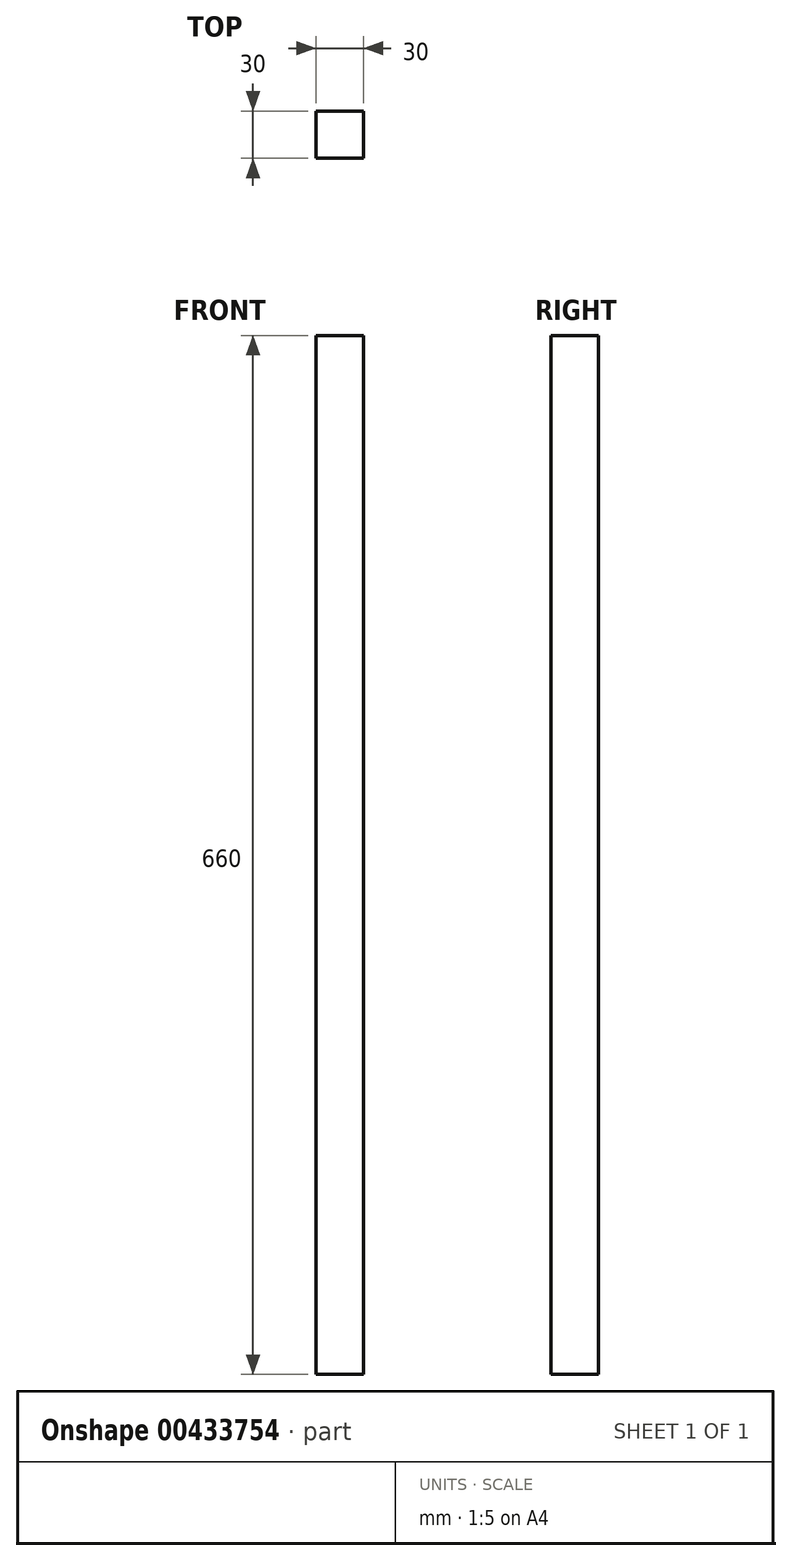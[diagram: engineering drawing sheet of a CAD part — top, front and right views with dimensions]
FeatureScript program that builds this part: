
annotation { "Feature Type Name" : "Feature", "Feature Type Description" : "" }
export const myFeature = defineFeature(function(context is Context, id is Id, definition is map)
    precondition{}
    {
        {
            var Q0;
            Q0=qCreatedBy(makeId("Front.planeOp"),FACE);
            var sketch = newSketch(context, id + "F0", { "sketchPlane" : qUnion([Q0])});
            skLineSegment(sketch, "E0.bottom", {"start": v(65.62, 660) * mm, "end": v(95.62, 660) * mm});
            skLineSegment(sketch, "E0.top", {"start": v(65.62, 0) * mm, "end": v(95.62, 0) * mm});
            skLineSegment(sketch, "E0.left", {"start": v(65.62, 660) * mm, "end": v(65.62, 0) * mm});
            skLineSegment(sketch, "E0.right", {"start": v(95.62, 660) * mm, "end": v(95.62, 0) * mm});
            skSolve(sketch);
        }
        {
            var Q0;
            Q0 = qSketchRegion(id + "F0", true);
            extrude(context, id + "F1", {"entities" : qUnion([Q0]), "depth" : 30 * mm, "offsetDistance" : 25 * mm});
        }
    });
